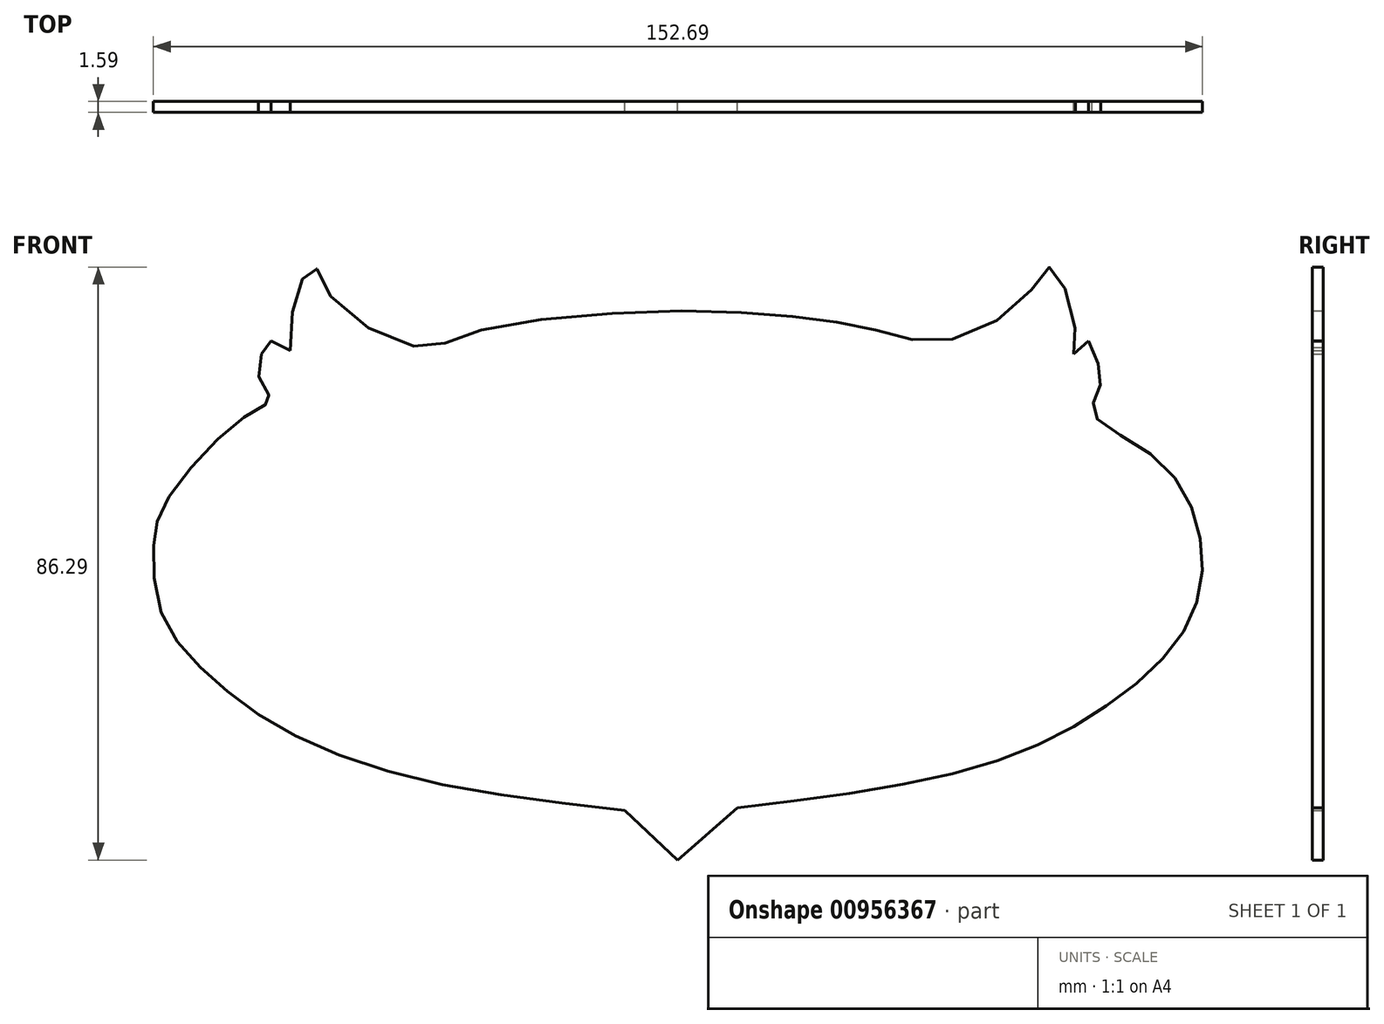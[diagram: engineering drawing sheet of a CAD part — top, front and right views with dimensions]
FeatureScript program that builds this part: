
annotation { "Feature Type Name" : "Feature", "Feature Type Description" : "" }
export const myFeature = defineFeature(function(context is Context, id is Id, definition is map)
    precondition{}
    {
        {
            var Q0;
            Q0=qCreatedBy(makeId("Front.planeOp"),FACE);
            var sketch = newSketch(context, id + "F0", { "sketchPlane" : qUnion([Q0])});
            skArc(sketch, "E0", {"start": v(-48.61, -17.82) * mm, "mid": v(-51.86, -24.98) * mm, "end": v(-51.62, -32.84) * mm});
            skLineSegment(sketch, "E1", {"start": v(-55.27, -31.23) * mm, "end": v(-51.62, -32.84) * mm});
            skLineSegment(sketch, "E2", {"start": v(-50, -16.63) * mm, "end": v(-48.61, -17.82) * mm});
            skLineSegment(sketch, "E3", {"start": v(-40.35, -22.54) * mm, "end": v(-35.77, -24.56) * mm});
            skLineSegment(sketch, "E4", {"start": v(-13.52, -36.7) * mm, "end": v(-10.65, -38.22) * mm});
            skLineSegment(sketch, "E5", {"start": v(14.91, -53.44) * mm, "end": v(11.46, -59.99) * mm});
            skLineSegment(sketch, "E6", {"start": v(14.91, -53.44) * mm, "end": v(19.85, -54.73) * mm});
            skLineSegment(sketch, "E7", {"start": v(19.85, -54.73) * mm, "end": v(17.81, -50.44) * mm});
            skLineSegment(sketch, "E8", {"start": v(55.9, -31.12) * mm, "end": v(52.13, -32.91) * mm});
            skLineSegment(sketch, "E9", {"start": v(48.93, -17.7) * mm, "end": v(50.22, -17.1) * mm});
            skLineSegment(sketch, "E10", {"start": v(40.99, -22.75) * mm, "end": v(35.7, -25.27) * mm});
            skLineSegment(sketch, "E11", {"start": v(27.25, -29.62) * mm, "end": v(19.85, -34.13) * mm});
            skLineSegment(sketch, "E12", {"start": v(14.27, -36.27) * mm, "end": v(10.51, -38.22) * mm});
            skLineSegment(sketch, "E13", {"start": v(6.86, -64.5) * mm, "end": v(1.07, -70.72) * mm});
            skLineSegment(sketch, "E14", {"start": v(1.07, -70.72) * mm, "end": v(-5.45, -64.65) * mm});
            skLineSegment(sketch, "E15", {"start": v(-7.73, -68.36) * mm, "end": v(0, -75.55) * mm});
            skLineSegment(sketch, "E16", {"start": v(0, -75.55) * mm, "end": v(8.69, -67.93) * mm});
            skLineSegment(sketch, "E17", {"start": v(59.77, 0) * mm, "end": v(57.61, -1.9) * mm});
            skLineSegment(sketch, "E18", {"start": v(58.37, -4.3) * mm, "end": v(52.26, -6.76) * mm});
            skArc(sketch, "E19", {"start": v(37.77, -3.76) * mm, "mid": v(46.25, -0.02) * mm, "end": v(53.54, 5.68) * mm});
            skArc(sketch, "E20", {"start": v(52.26, -6.76) * mm, "mid": v(54.6, -0.72) * mm, "end": v(53.54, 5.68) * mm});
            skArc(sketch, "E21", {"start": v(55.8, -11.06) * mm, "mid": v(57.79, -7.94) * mm, "end": v(58.37, -4.3) * mm});
            skArc(sketch, "E22", {"start": v(71.57, -27.9) * mm, "mid": v(65.35, -17.92) * mm, "end": v(55.8, -11.06) * mm});
            skArc(sketch, "E23", {"start": v(62.77, -48.3) * mm, "mid": v(70.55, -39.56) * mm, "end": v(71.57, -27.9) * mm});
            skArc(sketch, "E24", {"start": v(6.86, -64.5) * mm, "mid": v(36.1, -60.8) * mm, "end": v(62.77, -48.3) * mm});
            skArc(sketch, "E25", {"start": v(-59.13, -51.4) * mm, "mid": v(-33.18, -61.66) * mm, "end": v(-5.45, -64.65) * mm});
            skArc(sketch, "E26", {"start": v(-72.65, -32.3) * mm, "mid": v(-68.2, -43.5) * mm, "end": v(-59.13, -51.4) * mm});
            skArc(sketch, "E27", {"start": v(-65.46, -17.6) * mm, "mid": v(-70.52, -24.24) * mm, "end": v(-72.65, -32.3) * mm});
            skArc(sketch, "E28", {"start": v(-55.48, -10.41) * mm, "mid": v(-60.72, -13.66) * mm, "end": v(-65.46, -17.6) * mm});
            skArc(sketch, "E29", {"start": v(-57.52, -4.5) * mm, "mid": v(-57.77, -7.9) * mm, "end": v(-55.48, -10.41) * mm});
            skArc(sketch, "E30", {"start": v(-57.52, -4.5) * mm, "mid": v(-54.68, -6) * mm, "end": v(-51.5, -6.5) * mm});
            skArc(sketch, "E31", {"start": v(-53.7, 5.04) * mm, "mid": v(-53.47, -0.9) * mm, "end": v(-51.5, -6.5) * mm});
            skArc(sketch, "E32", {"start": v(37.77, -3.76) * mm, "mid": v(0.27, 1.25) * mm, "end": v(-37.13, -4.5) * mm});
            skArc(sketch, "E33", {"start": v(-53.7, 5.04) * mm, "mid": v(-45.6, -0.06) * mm, "end": v(-37.13, -4.5) * mm});
            skArc(sketch, "E34", {"start": v(0, -66) * mm, "mid": v(7.84, -51.99) * mm, "end": v(1.5, -37.24) * mm});
            skArc(sketch, "E35", {"start": v(-3.33, -40.13) * mm, "mid": v(-6.78, -53.72) * mm, "end": v(0, -66) * mm});
            skArc(sketch, "E36", {"start": v(-3.33, -40.13) * mm, "mid": v(-5, -51.28) * mm, "end": v(0, -61.38) * mm});
            skLineSegment(sketch, "E37", {"start": v(1.5, -37.24) * mm, "end": v(0, -61.38) * mm});
            skArc(sketch, "E38", {"start": v(11.46, -59.99) * mm, "mid": v(33.09, -55.78) * mm, "end": v(52.58, -45.5) * mm});
            skArc(sketch, "E39", {"start": v(52.58, -45.5) * mm, "mid": v(58.16, -37.1) * mm, "end": v(58.8, -27.04) * mm});
            skArc(sketch, "E40", {"start": v(58.8, -27.04) * mm, "mid": v(55.15, -21.52) * mm, "end": v(50.22, -17.1) * mm});
            skArc(sketch, "E41", {"start": v(52.13, -32.91) * mm, "mid": v(52.33, -24.93) * mm, "end": v(48.93, -17.7) * mm});
            skArc(sketch, "E42", {"start": v(33.58, -38.47) * mm, "mid": v(38.3, -32.45) * mm, "end": v(35.7, -25.27) * mm});
            skArc(sketch, "E43", {"start": v(14.27, -36.27) * mm, "mid": v(23.55, -40.69) * mm, "end": v(33.58, -38.47) * mm});
            skArc(sketch, "E44", {"start": v(10.51, -38.22) * mm, "mid": v(22.63, -43.16) * mm, "end": v(35.48, -40.69) * mm});
            skPoint(sketch, "E44.endSnap0", {"position": v(23.55, -40.69) * mm});
            skArc(sketch, "E45", {"start": v(35.48, -40.69) * mm, "mid": v(42.75, -33.1) * mm, "end": v(40.99, -22.75) * mm});
            skArc(sketch, "E46", {"start": v(19.85, -34.13) * mm, "mid": v(25.82, -35.6) * mm, "end": v(27.25, -29.62) * mm});
            skFitSpline(sketch, "E47", {"points": [v(-50.65, 0) * mm, v(-40.46, -7.62) * mm, v(-23.5, -13.74) * mm, v(-10.52, -21.03) * mm, v(-4.5, -26.61) * mm, v(-1.72, -34.56) * mm, v(-4.5, -32.3) * mm, v(-12.45, -26.4) * mm, v(-24.04, -20.82) * mm, v(-35.84, -16.1) * mm, v(-45.6, -9.66) * mm, v(-50.65, 0) * mm]});
            skFitSpline(sketch, "E48", {"points": [v(2.9, -33.37) * mm, v(5.9, -25.65) * mm, v(11.48, -20.6) * mm, v(20.28, -15.56) * mm, v(28.11, -12.02) * mm, v(40.24, -7.84) * mm, v(50.97, -0.97) * mm, v(46.35, -9.77) * mm, v(34.66, -16.63) * mm, v(20.81, -22) * mm, v(10.08, -27.58) * mm, v(2.9, -33.37) * mm]});
            skLineSegment(sketch, "E49", {"start": v(-26.4, -29.62) * mm, "end": v(-18.78, -33.8) * mm});
            skArc(sketch, "E50", {"start": v(-26.4, -29.62) * mm, "mid": v(-24.82, -35.78) * mm, "end": v(-18.78, -33.8) * mm});
            skFitSpline(sketch, "E51", {"points": [v(-40.35, -22.54) * mm, v(-42.39, -32.3) * mm, v(-35.63, -40.46) * mm, v(-20.07, -43.14) * mm, v(-10.65, -38.22) * mm], "startDerivative": vector(-16.71, -43.22) * mm, "endDerivative": vector(34.9, 26.26) * mm});
            skFitSpline(sketch, "E52", {"points": [v(-13.52, -36.7) * mm, v(-19.96, -40.67) * mm, v(-30.9, -40.03) * mm, v(-37.13, -33.27) * mm, v(-35.77, -24.56) * mm], "startDerivative": vector(-24.87, -20.73) * mm, "endDerivative": vector(12.32, 36.32) * mm});
            skFitSpline(sketch, "E53", {"points": [v(-50, -16.63) * mm, v(-58.7, -27.26) * mm, v(-56.87, -40.89) * mm, v(-45.29, -50.44) * mm, v(-35.77, -55.37) * mm, v(-22.54, -58.48) * mm, v(-9.45, -60.42) * mm, v(-9.34, -60.42) * mm], "startDerivative": vector(-65, -57.36) * mm, "endDerivative": vector(3.92, 0.5) * mm});
            skLineSegment(sketch, "E54", {"start": v(-13.42, -53.12) * mm, "end": v(-9.34, -60.42) * mm});
            skLineSegment(sketch, "E55", {"start": v(-13.42, -53.12) * mm, "end": v(-19.64, -54.73) * mm});
            skLineSegment(sketch, "E56", {"start": v(-19.64, -54.73) * mm, "end": v(-17.39, -50.11) * mm});
            skLineSegment(sketch, "E57", {"start": v(-59.24, 0) * mm, "end": v(-56.4, -1.43) * mm});
            skFitSpline(sketch, "E58", {"points": [v(-17.39, -50.11) * mm, v(-34.34, -50.27) * mm, v(-50.33, -42.6) * mm, v(-55.27, -36.06) * mm, v(-55.27, -31.23) * mm], "startDerivative": vector(-54.49, -6.64) * mm, "endDerivative": vector(4, 29.15) * mm});
            skFitSpline(sketch, "E59", {"points": [v(17.81, -50.44) * mm, v(32.83, -50.27) * mm, v(46.35, -45.5) * mm, v(54.83, -37.24) * mm, v(55.9, -31.12) * mm], "startDerivative": vector(53.28, -2.75) * mm, "endDerivative": vector(0.4, 32.87) * mm});
            skFitSpline(sketch, "E60", {"points": [v(8.69, -67.93) * mm, v(44.31, -61.81) * mm, v(63.3, -52.48) * mm, v(74.25, -41.2) * mm, v(76.04, -28.65) * mm, v(69.32, -16.85) * mm, v(60.41, -10.41) * mm, v(61.48, -6.33) * mm, v(59.77, 0) * mm], "startDerivative": vector(190.22, 22.78) * mm, "endDerivative": vector(-36.2, 77.17) * mm});
            skPoint(sketch, "E61.9.internal.snap0", {"position": v(58.69, -0.95) * mm});
            skFitSpline(sketch, "E61", {"points": [v(57.61, -1.9) * mm, v(57.61, 3.22) * mm, v(54.4, 10.72) * mm, v(51.07, 6.87) * mm, v(38.63, 0) * mm, v(29.08, 1.5) * mm, v(17.81, 3.43) * mm, v(-3.33, 4.29) * mm, v(-30.7, 0.96) * mm, v(-37.24, -0.95) * mm, v(-50.22, 6.11) * mm, v(-52.9, 10.72) * mm, v(-55.27, 7.62) * mm, v(-56.4, -1.43) * mm], "startDerivative": vector(11.26, 77.46) * mm, "endDerivative": vector(-3, -131.24) * mm});
            skFitSpline(sketch, "E62", {"points": [v(-59.24, 0) * mm, v(-60.63, -1.9) * mm, v(-60.63, -6.33) * mm, v(-59.24, -8.59) * mm, v(-60.95, -9.77) * mm, v(-68.14, -15.45) * mm, v(-75.12, -24.56) * mm, v(-76.28, -29.62) * mm, v(-75.22, -39.5) * mm, v(-69.32, -47.65) * mm, v(-59.24, -55.48) * mm, v(-39.7, -63.31) * mm, v(-7.73, -68.36) * mm], "startDerivative": vector(-36.48, -35.42) * mm, "endDerivative": vector(210.34, -24.28) * mm});
            skSolve(sketch);
        }
        {
            var Q0;
            Q0 = qSketchRegion(id + "F0", true);
            var Q1;
            Q1=makeQuery(id+"F0.imprint","IMPRINT",FACE,{"disambiguationData":[TD([[makeQuery(id+"F0.imprint","IMPRINT",EDGE,{"derivedFrom":sQuery(id+"F0.wireOp",EDGE,"E47")}),-1.0]])]});
            var Q2;
            Q2=makeQuery(id+"F0.imprint","IMPRINT",FACE,{"disambiguationData":[TD([[makeQuery(id+"F0.imprint","IMPRINT",EDGE,{"derivedFrom":sQuery(id+"F0.wireOp",EDGE,"E0")}),1.0]])]});
            var Q3;
            Q3=makeQuery(id+"F0.imprint","IMPRINT",FACE,{"disambiguationData":[TD([[makeQuery(id+"F0.imprint","IMPRINT",EDGE,{"derivedFrom":sQuery(id+"F0.wireOp",EDGE,"E3")}),-1.0]])]});
            var Q4;
            Q4=makeQuery(id+"F0.imprint","IMPRINT",FACE,{"disambiguationData":[TD([[makeQuery(id+"F0.imprint","IMPRINT",EDGE,{"derivedFrom":sQuery(id+"F0.wireOp",EDGE,"E49")}),-1.0]])]});
            var Q5;
            Q5=makeQuery(id+"F0.imprint","IMPRINT",FACE,{"disambiguationData":[TD([[makeQuery(id+"F0.imprint","IMPRINT",EDGE,{"derivedFrom":sQuery(id+"F0.wireOp",EDGE,"E11")}),1.0]])]});
            var Q6;
            Q6=makeQuery(id+"F0.imprint","IMPRINT",FACE,{"disambiguationData":[TD([[makeQuery(id+"F0.imprint","IMPRINT",EDGE,{"derivedFrom":sQuery(id+"F0.wireOp",EDGE,"E10")}),1.0]])]});
            var Q7;
            Q7=makeQuery(id+"F0.imprint","IMPRINT",FACE,{"disambiguationData":[TD([[makeQuery(id+"F0.imprint","IMPRINT",EDGE,{"derivedFrom":sQuery(id+"F0.wireOp",EDGE,"E48")}),-1.0]])]});
            var Q8;
            Q8=makeQuery(id+"F0.imprint","IMPRINT",FACE,{"disambiguationData":[TD([[makeQuery(id+"F0.imprint","IMPRINT",EDGE,{"derivedFrom":sQuery(id+"F0.wireOp",EDGE,"E0")}),-1.0]])]});
            var Q9;
            Q9=makeQuery(id+"F0.imprint","IMPRINT",FACE,{"disambiguationData":[TD([[makeQuery(id+"F0.imprint","IMPRINT",EDGE,{"derivedFrom":sQuery(id+"F0.wireOp",EDGE,"E34")}),1.0]])]});
            var Q10;
            Q10=makeQuery(id+"F0.imprint","IMPRINT",FACE,{"disambiguationData":[TD([[makeQuery(id+"F0.imprint","IMPRINT",EDGE,{"derivedFrom":sQuery(id+"F0.wireOp",EDGE,"E5")}),1.0]])]});
            extrude(context, id + "F1", {"entities" : qUnion([Q0, Q1, Q2, Q3, Q4, Q5, Q6, Q7, Q8, Q9, Q10]), "depth" : 1.59 * mm, "offsetDistance" : 25.4 * mm});
        }
        {
            var Q0;
            Q0=makeQuery(id+"F0.imprint","IMPRINT",FACE,{"disambiguationData":[TD([[makeQuery(id+"F0.imprint","IMPRINT",EDGE,{"derivedFrom":sQuery(id+"F0.wireOp",EDGE,"E13")}),1.0]])]});
            extrude(context, id + "F2", {"entities" : qUnion([Q0]), "operationType" : NewBodyOperationType.ADD, "depth" : 1.59 * mm, "offsetDistance" : 25.4 * mm});
        }
    });
